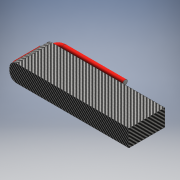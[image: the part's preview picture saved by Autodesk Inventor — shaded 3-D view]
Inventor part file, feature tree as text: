
AUTODESK INVENTOR PART (.ipt)
format: ipt  version: 2016 (Build 200138000, 138)  size: 228,352 bytes
history: native  units: mm
features: sketch x5, sweep x2, projected_geometry x2, extrude x1, fillet x1, plane x1
ambient origin geometry x8: Origin, YZ Plane, XZ Plane, XY Plane, X Axis, Y Axis, Z Axis, Center Point
bodies: Solid1 (feature_tree)
feature tree (12):
  extrude  "Extrusion1"  Depth=42.0mm
  sweep  "Sweep1"
  fillet  "Fillet1"  Radius=5.5mm
  plane  "Work Plane1"
  sweep  "Sweep2"
  sketch  "Sketch1"  dims[d0=140.0mm d1=42.0mm]
  sketch  "Sketch2"  dims[d2=20.0mm d3=0.0mm d4=5.5mm d5=5.5mm]
  projected_geometry  "Projected Loop1"
  sketch  "Sketch3"  dims[d6=7.0mm d7=0.0mm d8=0.0mm]
  sketch  "Sketch4"  dims[d9=8.0mm]
  projected_geometry  "Projected Loop2"
  sketch  "Sketch5"  dims[d10=1.5mm d11=1.5mm d12=0.75mm d13=1.5mm d14=0.0mm d15=0.0mm]
